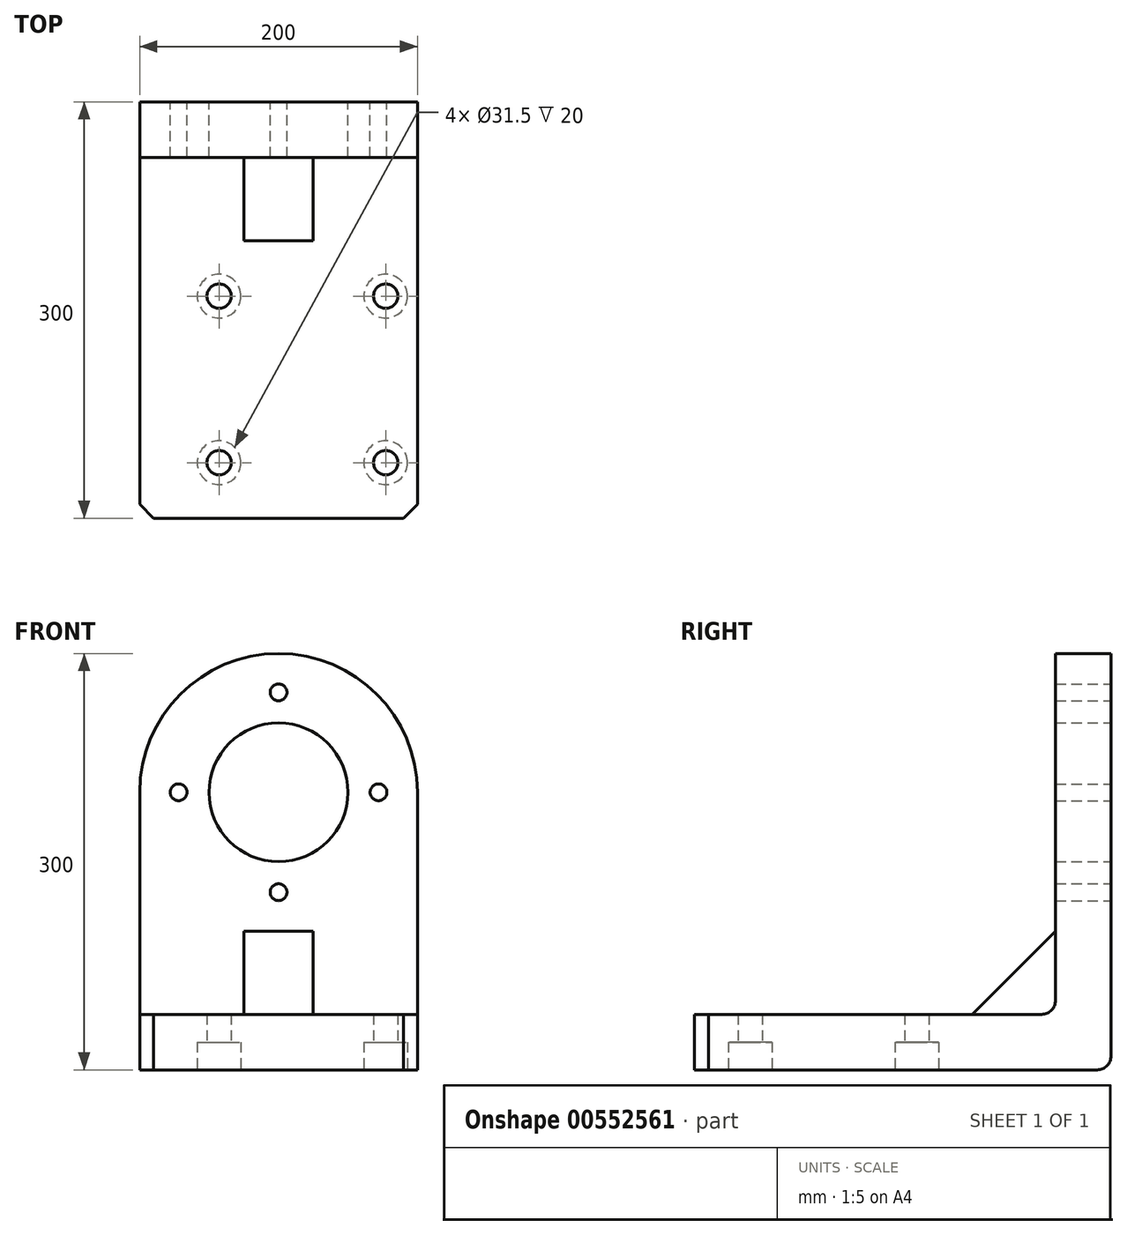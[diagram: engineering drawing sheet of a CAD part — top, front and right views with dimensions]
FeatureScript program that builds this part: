
annotation { "Feature Type Name" : "Feature", "Feature Type Description" : "" }
export const myFeature = defineFeature(function(context is Context, id is Id, definition is map)
    precondition{}
    {
        {
            var Q0;
            Q0=qCreatedBy(makeId("Front.planeOp"),FACE);
            var sketch = newSketch(context, id + "F0", { "sketchPlane" : qUnion([Q0])});
            skLineSegment(sketch, "E0", {"start": v(-100, 0) * mm, "end": v(-100, 200) * mm});
            skLineSegment(sketch, "E1.MirrorCS", {"start": v(100, 0) * mm, "end": v(100, 200) * mm});
            skLineSegment(sketch, "E2", {"start": v(-100, 200) * mm, "end": v(100, 200) * mm, "construction": true});
            skCircle(sketch, "E3", {"center": v(0, 200) * mm, "radius": 50 * mm});
            skLineSegment(sketch, "E4", {"start": v(-100, 200) * mm, "end": v(-100, 200) * mm});
            skArc(sketch, "E5", {"start": v(100, 200) * mm, "mid": v(0, 300) * mm, "end": v(-100, 200) * mm});
            skLineSegment(sketch, "E6", {"start": v(100, 200) * mm, "end": v(100, 200) * mm});
            skCircle(sketch, "E7", {"center": v(0, 200) * mm, "radius": 72 * mm, "construction": true});
            skLineSegment(sketch, "E8", {"start": v(-100, 0) * mm, "end": v(100, 0) * mm});
            skCircle(sketch, "E9", {"center": v(0, 272) * mm, "radius": 7 * mm});
            skCircle(sketch, "E10", {"center": v(0, 128) * mm, "radius": 7 * mm});
            skCircle(sketch, "E11", {"center": v(-72, 200) * mm, "radius": 7 * mm});
            skCircle(sketch, "E12", {"center": v(72, 200) * mm, "radius": 7 * mm});
            skLineSegment(sketch, "E13", {"start": v(0, 0) * mm, "end": v(0, 272) * mm, "construction": true});
            skLineSegment(sketch, "E14", {"start": v(-100, 40) * mm, "end": v(100, 40) * mm});
            skSolve(sketch);
        }
        {
            var Q0;
            Q0 = qSketchRegion(id + "F0", true);
            var Q1;
            Q1=makeQuery(id+"F0.imprint","IMPRINT",FACE,{"disambiguationData":[TD([[makeQuery(id+"F0.imprint","IMPRINT",EDGE,{"derivedFrom":sQuery(id+"F0.wireOp",EDGE,"E11")}),1.0]])]});
            var Q2;
            Q2=makeQuery(id+"F0.imprint","IMPRINT",FACE,{"disambiguationData":[TD([[makeQuery(id+"F0.imprint","IMPRINT",EDGE,{"derivedFrom":sQuery(id+"F0.wireOp",EDGE,"E9")}),1.0]])]});
            var Q3;
            Q3=makeQuery(id+"F0.imprint","IMPRINT",FACE,{"disambiguationData":[TD([[makeQuery(id+"F0.imprint","IMPRINT",EDGE,{"derivedFrom":sQuery(id+"F0.wireOp",EDGE,"E12")}),1.0]])]});
            var Q4;
            Q4=makeQuery(id+"F0.imprint","IMPRINT",FACE,{"disambiguationData":[TD([[makeQuery(id+"F0.imprint","IMPRINT",EDGE,{"derivedFrom":sQuery(id+"F0.wireOp",EDGE,"E10")}),1.0]])]});
            extrude(context, id + "F1", {"entities" : qUnion([Q0, Q1, Q2, Q3, Q4]), "depth" : 40 * mm, "offsetDistance" : 25 * mm});
        }
        {
            var Q0;
            Q0=sQuery(id+"F0.wireOp",VERTEX,"E13.end");
            var Q1;
            Q1=sQuery(id+"F0.wireOp",VERTEX,"E12.center");
            var Q2;
            Q2=sQuery(id+"F0.wireOp",VERTEX,"E10.center");
            var Q3;
            Q3=sQuery(id+"F0.wireOp",VERTEX,"E11.center");
            var Q4;
            Q4=makeQuery(id+"F1.opExtrude","SWEPT_BODY",BODY,{"disambiguationData":[OSD([sQuery(id+"F0.wireOp",EDGE,"E0"),sQuery(id+"F0.wireOp",EDGE,"E1.MirrorCS"),sQuery(id+"F0.wireOp",EDGE,"E3"),sQuery(id+"F0.wireOp",EDGE,"E5"),sQuery(id+"F0.wireOp",EDGE,"E8")])]});
            hole(context, id + "F2", {"style" : HoleStyle.SIMPLE, "endStyle" : HoleEndStyle.THROUGH, "oppositeDirection" : true, "standardTappedOrClearance" : lookupTablePath({ "standard" : "ISO", "engagement" : "75%", "pitch" : "2 mm", "size" : "M14", "type" : "Tapped" }), "standardBlindInLast" : lookupTablePath({ "standard" : "ISO", "engagement" : "75%", "pitch" : "2 mm", "size" : "M14", "type" : "Tapped" }), "holeDiameter" : 12.1 * mm, "showTappedDepth" : true, "isTappedThrough" : true, "tappedDepth" : 12 * mm, "tapClearance" : 3, "locations" : qUnion([Q0, Q1, Q2, Q3]), "scope" : qUnion([Q4]), "majorDiameter" : 14 * mm});
        }
        {
            var Q0;
            {var subQ0=sQuery(id+"F0.wireOp",EDGE,"E8");Q0=makeQuery(id+"F0.imprint","IMPRINT",FACE,{"disambiguationData":[TD([[makeQuery(id+"F0.imprint","IMPRINT",EDGE,{"derivedFrom":subQ0}),1.0]])]});}
            extrude(context, id + "F3", {"entities" : qUnion([Q0]), "operationType" : NewBodyOperationType.ADD, "depth" : 300 * mm, "offsetDistance" : 25 * mm});
        }
        {
            var Q0;
            Q0=qCreatedBy(makeId("Right.planeOp"),FACE);
            var sketch = newSketch(context, id + "F4", { "sketchPlane" : qUnion([Q0])});
            skLineSegment(sketch, "E15.0", {"start": v(-40, 40) * mm, "end": v(-40, 200) * mm});
            skLineSegment(sketch, "E16.0", {"start": v(-300, 40) * mm, "end": v(-40, 40) * mm});
            skLineSegment(sketch, "E17", {"start": v(-100, 40) * mm, "end": v(-40, 100) * mm});
            skSolve(sketch);
        }
        {
            var Q0;
            {var subQ3=sQuery(id+"F4.wireOp",EDGE,"E17");Q0=makeQuery(id+"F4.imprint","IMPRINT",FACE,{"disambiguationData":[TD([[makeQuery(id+"F4.imprint","IMPRINT",EDGE,{"derivedFrom":subQ3}),-1.0]])]});}
            extrude(context, id + "F5", {"entities" : qUnion([Q0]), "operationType" : NewBodyOperationType.ADD, "endBound" : BoundingType.SYMMETRIC, "depth" : 50 * mm, "offsetDistance" : 25 * mm});
        }
        {
            var Q0;
            Q0=qCreatedBy(makeId("Top.planeOp"),FACE);
            var sketch = newSketch(context, id + "F6", { "sketchPlane" : qUnion([Q0])});
            skLineSegment(sketch, "E18", {"start": v(-42.8, -140) * mm, "end": v(-42.8, -260) * mm, "construction": true});
            skLineSegment(sketch, "E19", {"start": v(-42.8, -260) * mm, "end": v(77.2, -260) * mm, "construction": true});
            skLineSegment(sketch, "E20", {"start": v(77.2, -260) * mm, "end": v(77.2, -140) * mm, "construction": true});
            skLineSegment(sketch, "E21", {"start": v(77.2, -140) * mm, "end": v(-42.8, -140) * mm, "construction": true});
            skCircle(sketch, "E22", {"center": v(77.2, -260) * mm, "radius": 8.75 * mm});
            skCircle(sketch, "E23", {"center": v(77.2, -140) * mm, "radius": 8.75 * mm});
            skCircle(sketch, "E24", {"center": v(-42.8, -140) * mm, "radius": 8.75 * mm});
            skCircle(sketch, "E25", {"center": v(-42.8, -260) * mm, "radius": 8.75 * mm});
            skSolve(sketch);
        }
        {
            var Q0;
            Q0=makeQuery(id+"F3.opExtrude","CAP_EDGE",EDGE,{"disambiguationData":[OSD([sQuery(id+"F0.wireOp",EDGE,"E0")])],"isStart":false});
            var Q1;
            Q1=makeQuery(id+"F3.opExtrude","CAP_EDGE",EDGE,{"disambiguationData":[OSD([sQuery(id+"F0.wireOp",EDGE,"E1.MirrorCS")])],"isStart":false});
            chamfer(context, id + "F7", {"entities" : qUnion([Q0, Q1]), "width" : 10 * mm, "tangentPropagation" : true});
        }
        {
            var Q0;
            {var subQ0=makeQuery(id+"F3.opExtrude","SWEPT_FACE",FACE,{"disambiguationData":[OSD([sQuery(id+"F0.wireOp",EDGE,"E14")])]});var subQ1=sQuery(id+"F0.wireOp",EDGE,"E0");var subQ2=makeQuery(id+"F1.opExtrude","CAP_FACE",FACE,{"disambiguationData":[OSD([subQ1,sQuery(id+"F0.wireOp",EDGE,"E1.MirrorCS"),sQuery(id+"F0.wireOp",EDGE,"E3"),sQuery(id+"F0.wireOp",EDGE,"E5"),sQuery(id+"F0.wireOp",EDGE,"E8")])],"isStart":false});Q0=makeQuery(id+"F5.boolean.opBoolean","SPLIT",EDGE,{"disambiguationData":[TD([makeQuery(id+"F1.opExtrude","SWEPT_FACE",FACE,{"disambiguationData":[OSD([subQ1])]})])],"derivedFrom":makeQuery(id+"F3.boolean.opBoolean","INTERSECT",EDGE,{"derivedFrom":[subQ2,subQ0]})});}
            var Q1;
            {var subQ0=makeQuery(id+"F3.opExtrude","SWEPT_FACE",FACE,{"disambiguationData":[OSD([sQuery(id+"F0.wireOp",EDGE,"E14")])]});var subQ1=sQuery(id+"F0.wireOp",EDGE,"E1.MirrorCS");var subQ2=makeQuery(id+"F1.opExtrude","CAP_FACE",FACE,{"disambiguationData":[OSD([sQuery(id+"F0.wireOp",EDGE,"E0"),subQ1,sQuery(id+"F0.wireOp",EDGE,"E3"),sQuery(id+"F0.wireOp",EDGE,"E5"),sQuery(id+"F0.wireOp",EDGE,"E8")])],"isStart":false});Q1=makeQuery(id+"F5.boolean.opBoolean","SPLIT",EDGE,{"disambiguationData":[TD([makeQuery(id+"F1.opExtrude","SWEPT_FACE",FACE,{"disambiguationData":[OSD([subQ1])]})])],"derivedFrom":makeQuery(id+"F3.boolean.opBoolean","INTERSECT",EDGE,{"derivedFrom":[subQ2,subQ0]})});}
            var Q2;
            Q2=makeQuery(id+"F1.opExtrude","CAP_EDGE",EDGE,{"disambiguationData":[OSD([sQuery(id+"F0.wireOp",EDGE,"E8")])],"isStart":true});
            fillet(context, id + "F8", {"entities" : qUnion([Q0, Q1, Q2]), "radius" : 10 * mm, "tangentPropagation" : true, "allowEdgeOverflow" : false});
        }
        {
            var Q0;
            Q0=sQuery(id+"F6.wireOp",VERTEX,"E25.center");
            var Q1;
            Q1=sQuery(id+"F6.wireOp",VERTEX,"E22.center");
            var Q2;
            Q2=sQuery(id+"F6.wireOp",VERTEX,"E23.center");
            var Q3;
            Q3=sQuery(id+"F6.wireOp",VERTEX,"E18.start");
            var Q4;
            Q4=makeQuery(id+"F1.opExtrude","SWEPT_BODY",BODY,{"disambiguationData":[OSD([sQuery(id+"F0.wireOp",EDGE,"E0"),sQuery(id+"F0.wireOp",EDGE,"E1.MirrorCS"),sQuery(id+"F0.wireOp",EDGE,"E3"),sQuery(id+"F0.wireOp",EDGE,"E5"),sQuery(id+"F0.wireOp",EDGE,"E8")])]});
            hole(context, id + "F9", {"style" : HoleStyle.C_BORE, "endStyle" : HoleEndStyle.THROUGH, "oppositeDirection" : true, "holeDiameter" : 17.5 * mm, "cBoreDiameter" : 31.5 * mm, "cBoreDepth" : 20 * mm, "isTappedThrough" : true, "tappedDepth" : 12 * mm, "tapClearance" : 3, "locations" : qUnion([Q0, Q1, Q2, Q3]), "scope" : qUnion([Q4])});
        }
    });
